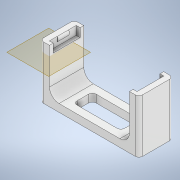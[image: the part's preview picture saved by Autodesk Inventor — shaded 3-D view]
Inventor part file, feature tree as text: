
AUTODESK INVENTOR PART (.ipt)
format: ipt  version: 2021 (Build 250183000, 183)  size: 227,840 bytes
history: mixed  units: in
note: dims shown in document units (in); Inventor stores cm internally (conversion verified against a paired STEP export)
features: projected_geometry x6, extrude x5, sketch x5, fillet x2, mirror x1, plane x1, imported_body x1
ambient origin geometry x8: Origin, YZ Plane, XZ Plane, XY Plane, X Axis, Y Axis, Z Axis, Center Point
bodies: Solid1 (imported_parasolid)
feature tree (21):
  extrude  "Extrusion1"  Depth=0.0984in
  extrude  "Extrusion2"  Depth=0.2362in
  mirror  "Mirror1"
  extrude  "Extrusion3"  Depth=0.3937in TaperAngle=0.0deg
  extrude  "Extrusion4"  Depth=0.1969in
  fillet  "Fillet4"  Radius=0.0197in
  plane  "Work Plane1"
  extrude  "Extrusion6"  Depth=0.2362in
  sketch  "Sketch1"  dims[d0=0.0984in d1=0.0in d3=0.0984in]
  projected_geometry  "Projected Loop1"
  projected_geometry  "Projected Loop2"
  sketch  "Sketch2"  dims[d4=0.2362in d5=0.0in d7=0.0394in]
  projected_geometry  "Projected Loop3"
  sketch  "Sketch3"  dims[d8=0.0394in d9=0.3937in d10=0.7874in d11=0.0in d12=0.0in]
  sketch  "Sketch4"  dims[d14=0.0394in d15=0.0in d16=0.1969in d22=0.0197in d23=0.0in]
  projected_geometry  "Projected Loop4"
  sketch  "Sketch7"  dims[d24=0.0197in d25=0.2362in d17=0.0197in d18=0.0344in d19=0.0197in d20=0.0344in]
  projected_geometry  "Projected Loop5"
  projected_geometry  "Projected Loop6"
  fillet  "Fillet2"  Radius=0.0197in
  imported_body  NMx_Import_Brep_tag  [imported B-rep: ~38 faces, bbox_mm=[52.0, 28.0, 18.0]]
